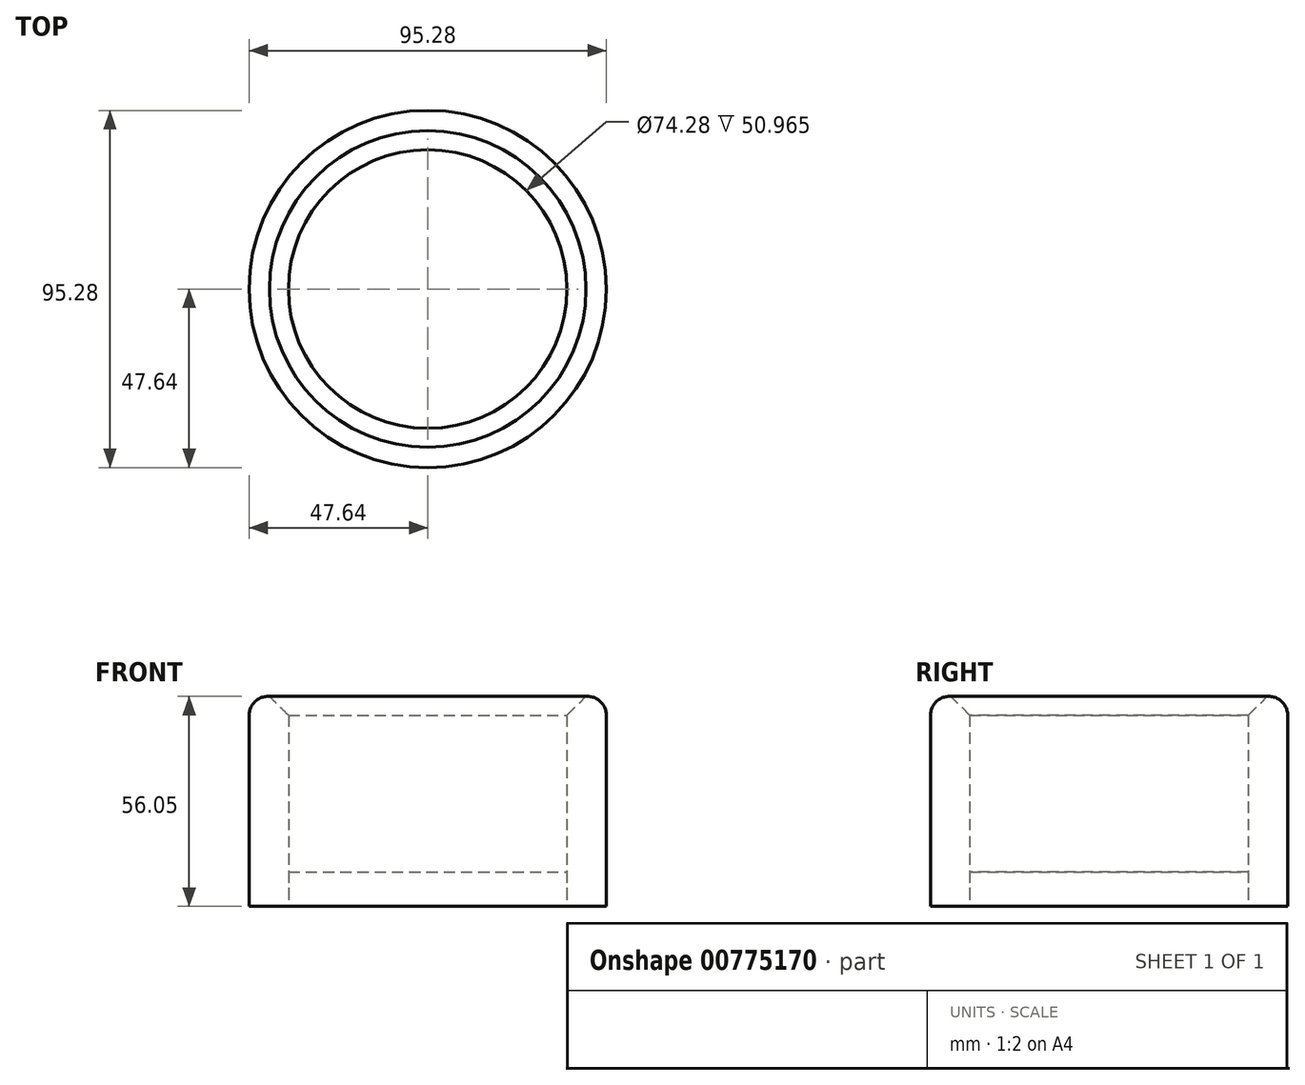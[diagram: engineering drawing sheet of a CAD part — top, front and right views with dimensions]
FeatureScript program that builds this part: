
annotation { "Feature Type Name" : "Feature", "Feature Type Description" : "" }
export const myFeature = defineFeature(function(context is Context, id is Id, definition is map)
    precondition{}
    {
        {
            var Q0;
            Q0=qCreatedBy(makeId("Right.planeOp"),FACE);
            var sketch = newSketch(context, id + "F0", { "sketchPlane" : qUnion([Q0])});
            skLineSegment(sketch, "E0", {"start": v(-47.64, 56.05) * mm, "end": v(-47.64, 0) * mm});
            skLineSegment(sketch, "E1", {"start": v(-47.64, 0) * mm, "end": v(-37.14, 0) * mm});
            skLineSegment(sketch, "E2", {"start": v(-37.14, 0) * mm, "end": v(-37.14, 56.05) * mm});
            skLineSegment(sketch, "E3", {"start": v(-37.14, 56.05) * mm, "end": v(-47.64, 56.05) * mm});
            skSolve(sketch);
        }
        {
            var Q0;
            Q0=makeQuery(id+"F0.imprint","IMPRINT",FACE,{"disambiguationData":[TD([[makeQuery(id+"F0.imprint","IMPRINT",EDGE,{"derivedFrom":sQuery(id+"F0.wireOp",EDGE,"E0")}),1.0]])]});
            var sketch = newSketch(context, id + "F1", { "sketchPlane" : qUnion([Q0])});
            skLineSegment(sketch, "E4.bottom", {"start": v(-37.31, 0) * mm, "end": v(0, 0) * mm});
            skLineSegment(sketch, "E4.top", {"start": v(-37.31, 9.26) * mm, "end": v(0, 9.26) * mm});
            skLineSegment(sketch, "E4.left", {"start": v(-37.31, 0) * mm, "end": v(-37.31, 9.26) * mm});
            skLineSegment(sketch, "E4.right", {"start": v(0, 0) * mm, "end": v(0, 9.26) * mm});
            skSolve(sketch);
        }
        {
            var Q0;
            {var subQ3=sQuery(id+"F1.wireOp",EDGE,"E4.right");Q0=makeQuery(id+"F1.imprint","IMPRINT",FACE,{"disambiguationData":[TD([[makeQuery(id+"F1.imprint","IMPRINT",EDGE,{"derivedFrom":subQ3}),1.0]])]});}
            var Q1;
            Q1=makeQuery(id+"F0.imprint","IMPRINT",FACE,{"disambiguationData":[TD([[makeQuery(id+"F0.imprint","IMPRINT",EDGE,{"derivedFrom":sQuery(id+"F0.wireOp",EDGE,"E0")}),1.0]])]});
            var Q2;
            Q2=sQuery(id+"F1.wireOp",EDGE,"E4.right");
            revolve(context, id + "F2", {"surfaceOperationType" : NewSurfaceOperationType.NEW, "entities" : qUnion([Q0, Q1]), "axis" : qUnion([Q2]), "revolveType" : RevolveType.FULL});
        }
        {
            var Q0;
            Q0=makeQuery(id+"F2.opRevolve","SWEPT_EDGE",EDGE,{"disambiguationData":[OSD([sQuery(id+"F0.wireOp",EDGE,"E2"),sQuery(id+"F0.wireOp",EDGE,"E3")])]});
            chamfer(context, id + "F3", {"entities" : qUnion([Q0]), "width" : 5.08 * mm, "tangentPropagation" : true});
        }
        {
            var Q0;
            Q0=makeQuery(id+"F2.opRevolve","SWEPT_EDGE",EDGE,{"disambiguationData":[OSD([sQuery(id+"F0.wireOp",EDGE,"E0"),sQuery(id+"F0.wireOp",EDGE,"E3")])]});
            fillet(context, id + "F4", {"entities" : qUnion([Q0]), "radius" : 5.08 * mm, "tangentPropagation" : true, "allowEdgeOverflow" : false});
        }
    });
